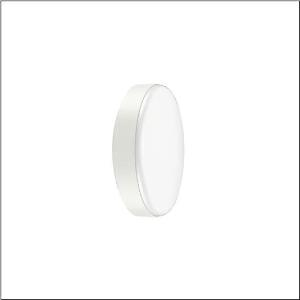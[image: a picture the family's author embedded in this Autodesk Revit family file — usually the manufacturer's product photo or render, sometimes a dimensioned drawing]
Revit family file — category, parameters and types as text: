
# Revit family: rondel_31_51wc10ma32as
name_source: partatom
category: Lighting Fixtures
units: mm (PartAtom-declared; Revit-internal decimal feet)

## family parameters
Cut with Voids When Loaded = No
Host = Face
Light Source = No
Part Type = Normal
Room Calculation Point = No
Round Connector Dimension = Use Diameter
Shared = No

## types (1)
- --- (1 x LED, 2450 lm, 20.4 W, 3000K)
    Apparent Load = 20 VA
    CIE Flux Codes = 44 75 94 94 100
    Color Rendering = 80
    Color Temperature = 3000K
    Default Elevation = 1800 mm
    Description = Rondel 31, wall and ceiling luminaire, primary optical cover: cover, of PC, opal, light emission: direct distribution, primary light characteristic: symmetric, installation type: surface-mounted, LED, rated luminous flux: 2.450lm, luminous efficacy: 120lm/W, light colour: 830, colour temperature: 3000K, with terminal, 3-pole, max. 2.5mm², mains connection: 220..240V, AC, 50/60Hz, rated input power: 20.5W, luminaire housing, of PC, traffic white (RAL 9016), diameter: 350mm, brightness and presence sensor, HF sensor, protection rating (complete): IP65, insulation class (complete): insulation class II (safety insulation), certification: CE, impact resistance: IK10, permissible operating ambient temperature: -20..+40°C, permissible storage temperature: -20..+60°C, packaging unit: 1 piece
    Height = 97 mm
    Lamp = 1 x LED
    Lamp Light Flux = 2450 lm
    Lamp Power = 20.4 W
    Lamp count = 1
    Length = 350 mm
    Luminous efficacy = 120 lm/W
    Manufacturer = Siteco
    ModVariant = No
    Model = 51WC10MA32AS
    Mounting Place = Ceiling
    Mounting Type = Surface mounted
    Number of Poles = 1
    OnlyDefault = Yes
    Power Factor = 1
    Product Name = Rondel 31
    Product group = wall and ceiling luminaire
    ProductGroupID = 301
    Protection Class = Protection class II
    Protection Degree = IP 65
    RLX_Detail_Level = 1
    RLX_Emergency_Light_Flux = 0 lm
    RLX_Emergency_Type = 0
    RLX_Emergency_Type_DB = No
    RlxData = <blob elided: 30465 chars, md5=c71b4578>
    Socket = socket
    Standby Power = 0 W
    System Light Flux = 2450 lm
    System Power = 20 W
    Type Comments = factory setting: luminous flux: 100 % | (ON | ON)
    Type Image = l_1007027.jpg
    URL = http://relux.com
    VarID = @adj_041941
    Voltage = 0 V
    Weight = 0.00 kg
    Width = 0 mm  [stored 0 ft]

note: [stored X ft] marks values corroborated as IEEE doubles in the binary element streams (Revit-internal decimal feet)

## geometry (parser evidence)
native form markers: Blend x4, Sweep x14
no freeform markers — native parametric forms only
